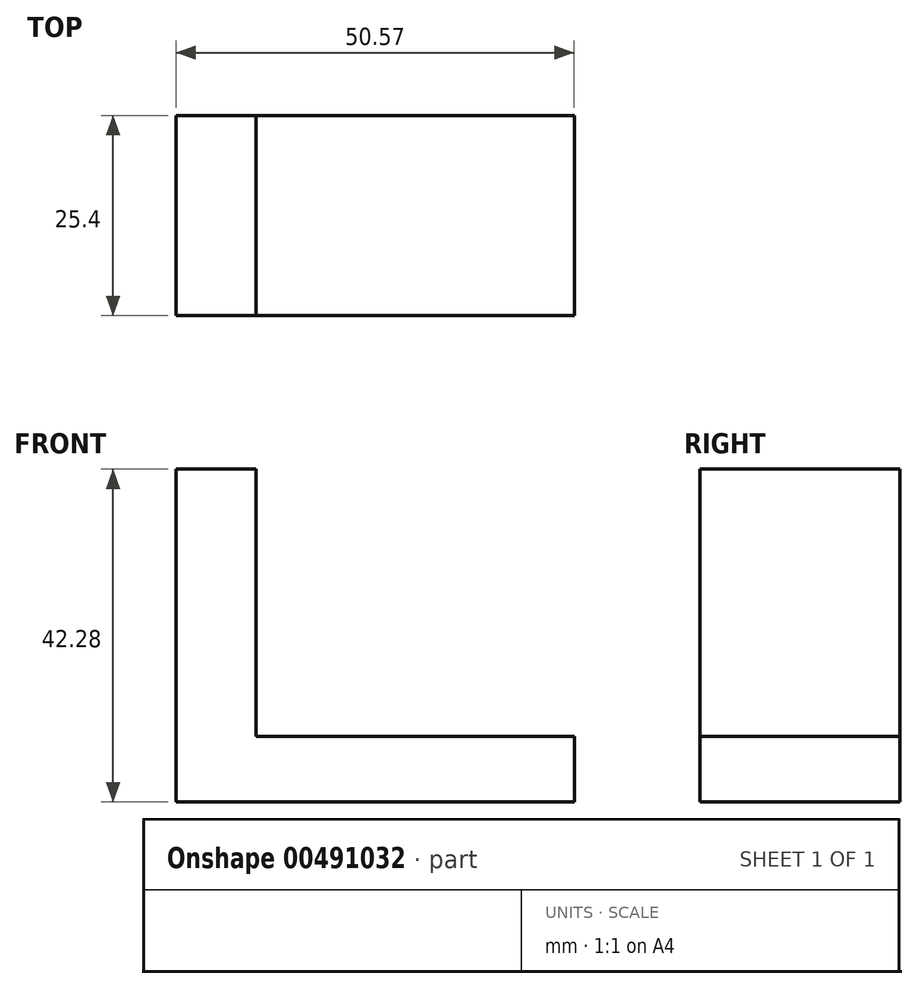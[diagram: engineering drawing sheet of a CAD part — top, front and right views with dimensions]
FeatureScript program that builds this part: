
annotation { "Feature Type Name" : "Feature", "Feature Type Description" : "" }
export const myFeature = defineFeature(function(context is Context, id is Id, definition is map)
    precondition{}
    {
        {
            var Q0;
            Q0=qCreatedBy(makeId("Front.planeOp"),FACE);
            var sketch = newSketch(context, id + "F0", { "sketchPlane" : qUnion([Q0])});
            skLineSegment(sketch, "E0", {"start": v(0, 0) * mm, "end": v(0, 42.28) * mm});
            skLineSegment(sketch, "E1", {"start": v(10.17, 42.28) * mm, "end": v(10.17, 8.3) * mm});
            skLineSegment(sketch, "E2", {"start": v(10.17, 8.3) * mm, "end": v(50.57, 8.3) * mm});
            skLineSegment(sketch, "E3", {"start": v(50.57, 8.3) * mm, "end": v(50.57, 0) * mm});
            skLineSegment(sketch, "E4", {"start": v(50.57, 0) * mm, "end": v(0, 0) * mm});
            skLineSegment(sketch, "E5", {"start": v(0, 42.28) * mm, "end": v(10.17, 42.28) * mm});
            skSolve(sketch);
        }
        {
            var Q0;
            Q0=makeQuery(id+"F0.imprint","IMPRINT",FACE,{"disambiguationData":[TD([[makeQuery(id+"F0.imprint","IMPRINT",EDGE,{"derivedFrom":sQuery(id+"F0.wireOp",EDGE,"E0")}),-1.0]])]});
            extrude(context, id + "F1", {"entities" : qUnion([Q0]), "depth" : 25.4 * mm});
        }
    });
